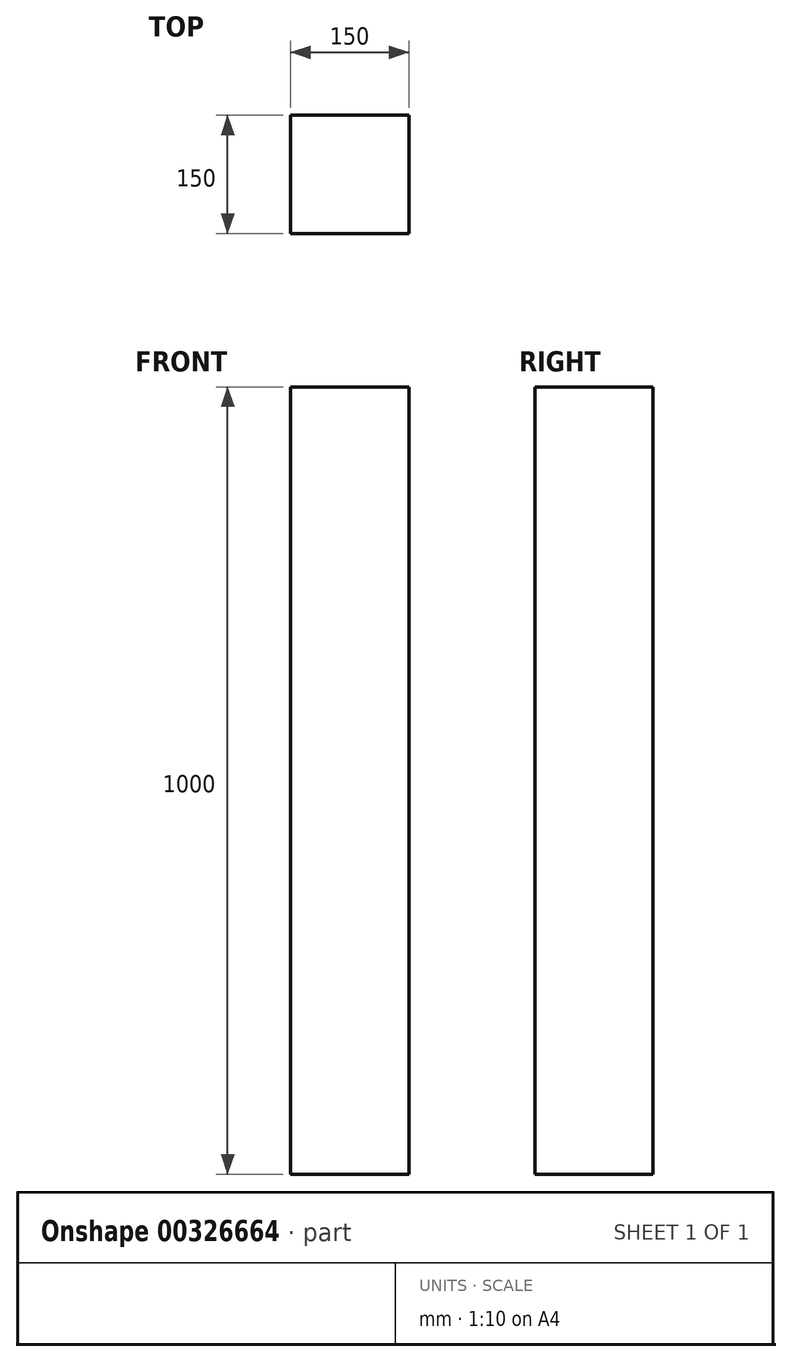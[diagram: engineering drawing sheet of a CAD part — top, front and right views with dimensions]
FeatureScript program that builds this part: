
annotation { "Feature Type Name" : "Feature", "Feature Type Description" : "" }
export const myFeature = defineFeature(function(context is Context, id is Id, definition is map)
    precondition{}
    {
        {
            var Q0;
            Q0=qCreatedBy(makeId("Top.planeOp"),FACE);
            var sketch = newSketch(context, id + "F0", { "sketchPlane" : qUnion([Q0])});
            skLineSegment(sketch, "E0.bottom", {"start": v(0, 0) * mm, "end": v(150, 0) * mm});
            skLineSegment(sketch, "E0.top", {"start": v(0, 150) * mm, "end": v(150, 150) * mm});
            skLineSegment(sketch, "E0.left", {"start": v(0, 0) * mm, "end": v(0, 150) * mm});
            skLineSegment(sketch, "E0.right", {"start": v(150, 0) * mm, "end": v(150, 150) * mm});
            skSolve(sketch);
        }
        {
            var Q0;
            Q0 = qSketchRegion(id + "F0", true);
            extrude(context, id + "F1", {"entities" : qUnion([Q0]), "depth" : 1000 * mm});
        }
    });
